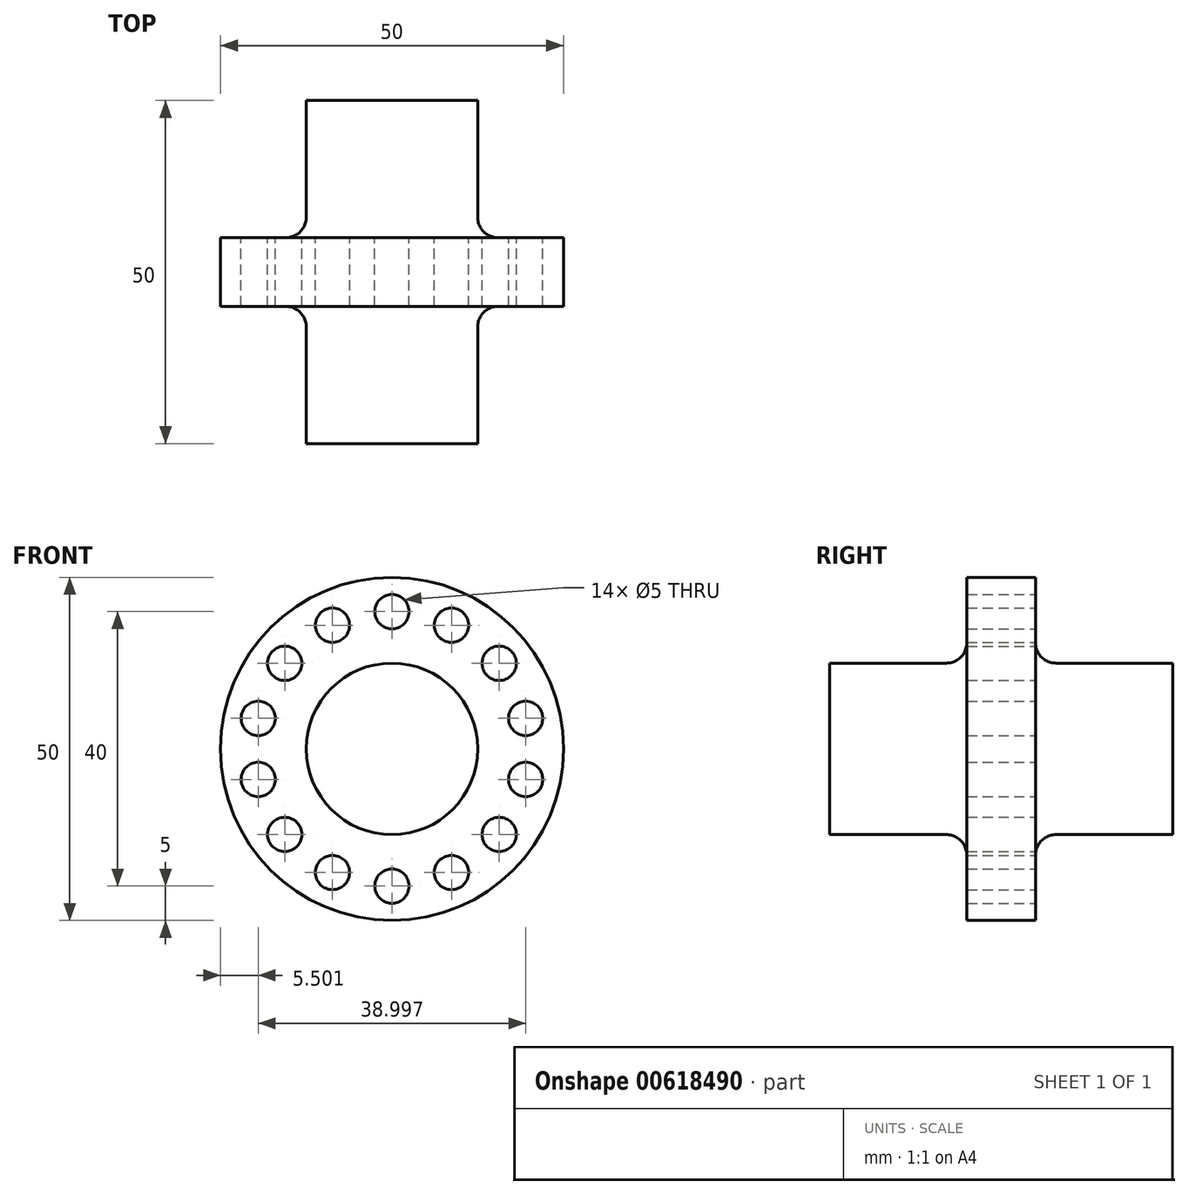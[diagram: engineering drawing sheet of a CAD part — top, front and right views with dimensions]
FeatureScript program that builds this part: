
annotation { "Feature Type Name" : "Feature", "Feature Type Description" : "" }
export const myFeature = defineFeature(function(context is Context, id is Id, definition is map)
    precondition{}
    {
        {
            var Q0;
            Q0=qCreatedBy(makeId("Front.planeOp"),FACE);
            var sketch = newSketch(context, id + "F0", { "sketchPlane" : qUnion([Q0])});
            skCircle(sketch, "E0", {"center": v(0, 0) * mm, "radius": 12.5 * mm});
            skSolve(sketch);
        }
        {
            var Q0;
            Q0=makeQuery(id+"F0.imprint","IMPRINT",FACE,{"disambiguationData":[TD([[makeQuery(id+"F0.imprint","IMPRINT",EDGE,{"derivedFrom":sQuery(id+"F0.wireOp",EDGE,"E0")}),1.0]])]});
            extrude(context, id + "F1", {"entities" : qUnion([Q0]), "endBound" : BoundingType.SYMMETRIC, "depth" : 50 * mm, "offsetDistance" : 25 * mm});
        }
        {
            var Q0;
            Q0=qCreatedBy(makeId("Front.planeOp"),FACE);
            var sketch = newSketch(context, id + "F2", { "sketchPlane" : qUnion([Q0])});
            skCircle(sketch, "E1", {"center": v(0, 0) * mm, "radius": 25 * mm});
            skCircle(sketch, "E2", {"center": v(0, 0) * mm, "radius": 20 * mm, "construction": true});
            skCircle(sketch, "E3", {"center": v(0, 20) * mm, "radius": 2.5 * mm});
            skCircle(sketch, "E4.1.0", {"center": v(-8.68, 18.02) * mm, "radius": 2.5 * mm});
            skCircle(sketch, "E4.2.0", {"center": v(-15.64, 12.47) * mm, "radius": 2.5 * mm});
            skCircle(sketch, "E5.1.3.0", {"center": v(-19.5, 4.45) * mm, "radius": 2.5 * mm});
            skCircle(sketch, "E5.1.4.0", {"center": v(-19.5, -4.45) * mm, "radius": 2.5 * mm});
            skCircle(sketch, "E5.1.5.0", {"center": v(-15.64, -12.47) * mm, "radius": 2.5 * mm});
            skCircle(sketch, "E5.1.6.0", {"center": v(-8.68, -18.02) * mm, "radius": 2.5 * mm});
            skCircle(sketch, "E5.1.7.0", {"center": v(0, -20) * mm, "radius": 2.5 * mm});
            skCircle(sketch, "E5.1.8.0", {"center": v(8.68, -18.02) * mm, "radius": 2.5 * mm});
            skCircle(sketch, "E5.1.9.0", {"center": v(15.64, -12.47) * mm, "radius": 2.5 * mm});
            skCircle(sketch, "E5.1.10.0", {"center": v(19.5, -4.45) * mm, "radius": 2.5 * mm});
            skCircle(sketch, "E5.1.11.0", {"center": v(19.5, 4.45) * mm, "radius": 2.5 * mm});
            skCircle(sketch, "E6.1.12.0", {"center": v(15.64, 12.47) * mm, "radius": 2.5 * mm});
            skCircle(sketch, "E6.1.13.0", {"center": v(8.68, 18.02) * mm, "radius": 2.5 * mm});
            skSolve(sketch);
        }
        {
            var Q0;
            Q0=makeQuery(id+"F2.imprint","IMPRINT",FACE,{"disambiguationData":[TD([[makeQuery(id+"F2.imprint","IMPRINT",EDGE,{"derivedFrom":sQuery(id+"F2.wireOp",EDGE,"E1")}),1.0]])]});
            extrude(context, id + "F3", {"entities" : qUnion([Q0]), "operationType" : NewBodyOperationType.ADD, "endBound" : BoundingType.SYMMETRIC, "depth" : 10 * mm, "offsetDistance" : 25 * mm});
        }
        {
            var Q0;
            Q0=makeQuery(id+"F3.boolean.opBoolean","INTERSECT",EDGE,{"derivedFrom":[makeQuery(id+"F1.opExtrude","SWEPT_FACE",FACE,{"disambiguationData":[OSD([sQuery(id+"F0.wireOp",EDGE,"E0")])]}),makeQuery(id+"F3.opExtrude","CAP_FACE",FACE,{"disambiguationData":[OSD([sQuery(id+"F2.wireOp",EDGE,"E1"),sQuery(id+"F2.wireOp",EDGE,"E3"),sQuery(id+"F2.wireOp",EDGE,"E4.1.0"),sQuery(id+"F2.wireOp",EDGE,"E4.2.0"),sQuery(id+"F2.wireOp",EDGE,"E5.1.3.0"),sQuery(id+"F2.wireOp",EDGE,"E5.1.4.0"),sQuery(id+"F2.wireOp",EDGE,"E5.1.5.0"),sQuery(id+"F2.wireOp",EDGE,"E5.1.6.0"),sQuery(id+"F2.wireOp",EDGE,"E5.1.7.0"),sQuery(id+"F2.wireOp",EDGE,"E5.1.8.0"),sQuery(id+"F2.wireOp",EDGE,"E5.1.9.0"),sQuery(id+"F2.wireOp",EDGE,"E5.1.10.0"),sQuery(id+"F2.wireOp",EDGE,"E5.1.11.0"),sQuery(id+"F2.wireOp",EDGE,"E6.1.12.0"),sQuery(id+"F2.wireOp",EDGE,"E6.1.13.0")])],"isStart":true})]});
            var Q1;
            Q1=makeQuery(id+"F3.boolean.opBoolean","INTERSECT",EDGE,{"derivedFrom":[makeQuery(id+"F1.opExtrude","SWEPT_FACE",FACE,{"disambiguationData":[OSD([sQuery(id+"F0.wireOp",EDGE,"E0")])]}),makeQuery(id+"F3.opExtrude","CAP_FACE",FACE,{"disambiguationData":[OSD([sQuery(id+"F2.wireOp",EDGE,"E1"),sQuery(id+"F2.wireOp",EDGE,"E3"),sQuery(id+"F2.wireOp",EDGE,"E4.1.0"),sQuery(id+"F2.wireOp",EDGE,"E4.2.0"),sQuery(id+"F2.wireOp",EDGE,"E5.1.3.0"),sQuery(id+"F2.wireOp",EDGE,"E5.1.4.0"),sQuery(id+"F2.wireOp",EDGE,"E5.1.5.0"),sQuery(id+"F2.wireOp",EDGE,"E5.1.6.0"),sQuery(id+"F2.wireOp",EDGE,"E5.1.7.0"),sQuery(id+"F2.wireOp",EDGE,"E5.1.8.0"),sQuery(id+"F2.wireOp",EDGE,"E5.1.9.0"),sQuery(id+"F2.wireOp",EDGE,"E5.1.10.0"),sQuery(id+"F2.wireOp",EDGE,"E5.1.11.0"),sQuery(id+"F2.wireOp",EDGE,"E6.1.12.0"),sQuery(id+"F2.wireOp",EDGE,"E6.1.13.0")])],"isStart":false})]});
            fillet(context, id + "F4", {"entities" : qUnion([Q0, Q1]), "radius" : 3 * mm, "tangentPropagation" : true, "allowEdgeOverflow" : false});
        }
    });
